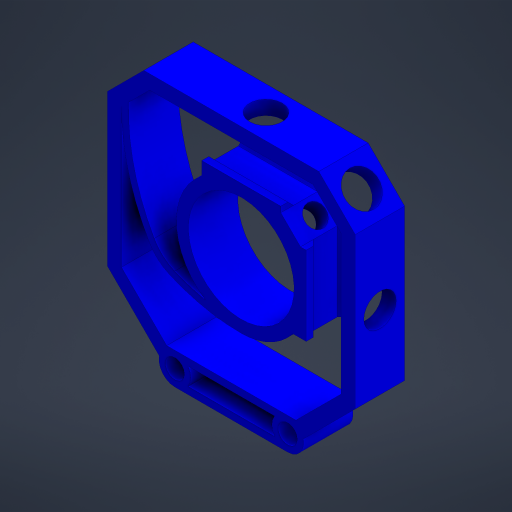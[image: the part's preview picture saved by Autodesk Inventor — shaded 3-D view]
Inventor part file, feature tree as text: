
AUTODESK INVENTOR PART (.ipt)
format: ipt  version: 2023.4 (Build 274418000, 418)  size: 404,992 bytes
history: native  units: mm
features: extrude x6, projected_geometry x4, reference x3, other x2, plane x1, mirror x1, sketch x1
ambient origin geometry x8: Origin, YZ Plane, XZ Plane, XY Plane, X Axis, Y Axis, Z Axis, Center Point
bodies: Solid1 (feature_tree)
feature tree (18):
  extrude  "Extrusion1"  Depth=10.0mm
  extrude  "Extrusion2"  Depth=10.0mm
  extrude  "Extrusion3"  TaperAngle=45.0deg  [1 undecoded]
  extrude  "Extrusion4"  Depth=10.0mm
  plane  "Work Plane1"
  mirror  "Mirror1"
  extrude  "Extrusion5"  Depth=10.0mm
  extrude  "Extrusion6"  Depth=10.0mm
  sketch  "Sketch1"  dims[d0=1.25mm d1=1.25mm d2=2.5mm d3=45.0deg d4=18.75mm d5=2.5mm d6=2.125mm d7=1.25mm d8=14.0mm d9=2.5mm d10=0.625mm d11=5.0mm d12=135.0deg d13=3.0mm d14=2.0mm d15=2.0mm d16=38.935534mm d17=38.935534mm d18=9.25mm d19=9.25mm d20=9.25mm d21=9.25mm d22=5.0mm d23=5.0mm d24=5.0mm d25=5.0mm d26=2.5mm d28=8.75mm d29=0.0mm d30=1.875mm d31=1.25mm d32=0.0mm d33=5.75mm d34=10.0mm d35=0.0mm d36=1.25mm d37=135.0deg d38=10.0mm d39=0.0mm d40=3.75mm d41=6.0mm d42=10.0mm d43=0.0mm d44=10.0mm d45=0.0mm d46=0.1425mm d47=0.1445mm d48=15.0mm d49=3.75mm d50=1.25mm d51=2.5mm d52=2.5mm]
  reference  "Reference1"
  reference  "Reference2"
  reference  "Reference3"
  projected_geometry  "Projected Loop1"
  projected_geometry  "Projected Loop2"
  projected_geometry  "Projected Loop3"
  projected_geometry  "Projected Loop4"
  other  "Cube 1x1 V5.iam"
  other  "Cube 1x1 Bottom V5:1"
note: 1 required parameter value undecoded (feature->parameter linkage not recoverable at this tier; creation-order binding heuristic only, values carry confidence <= 0.55)
